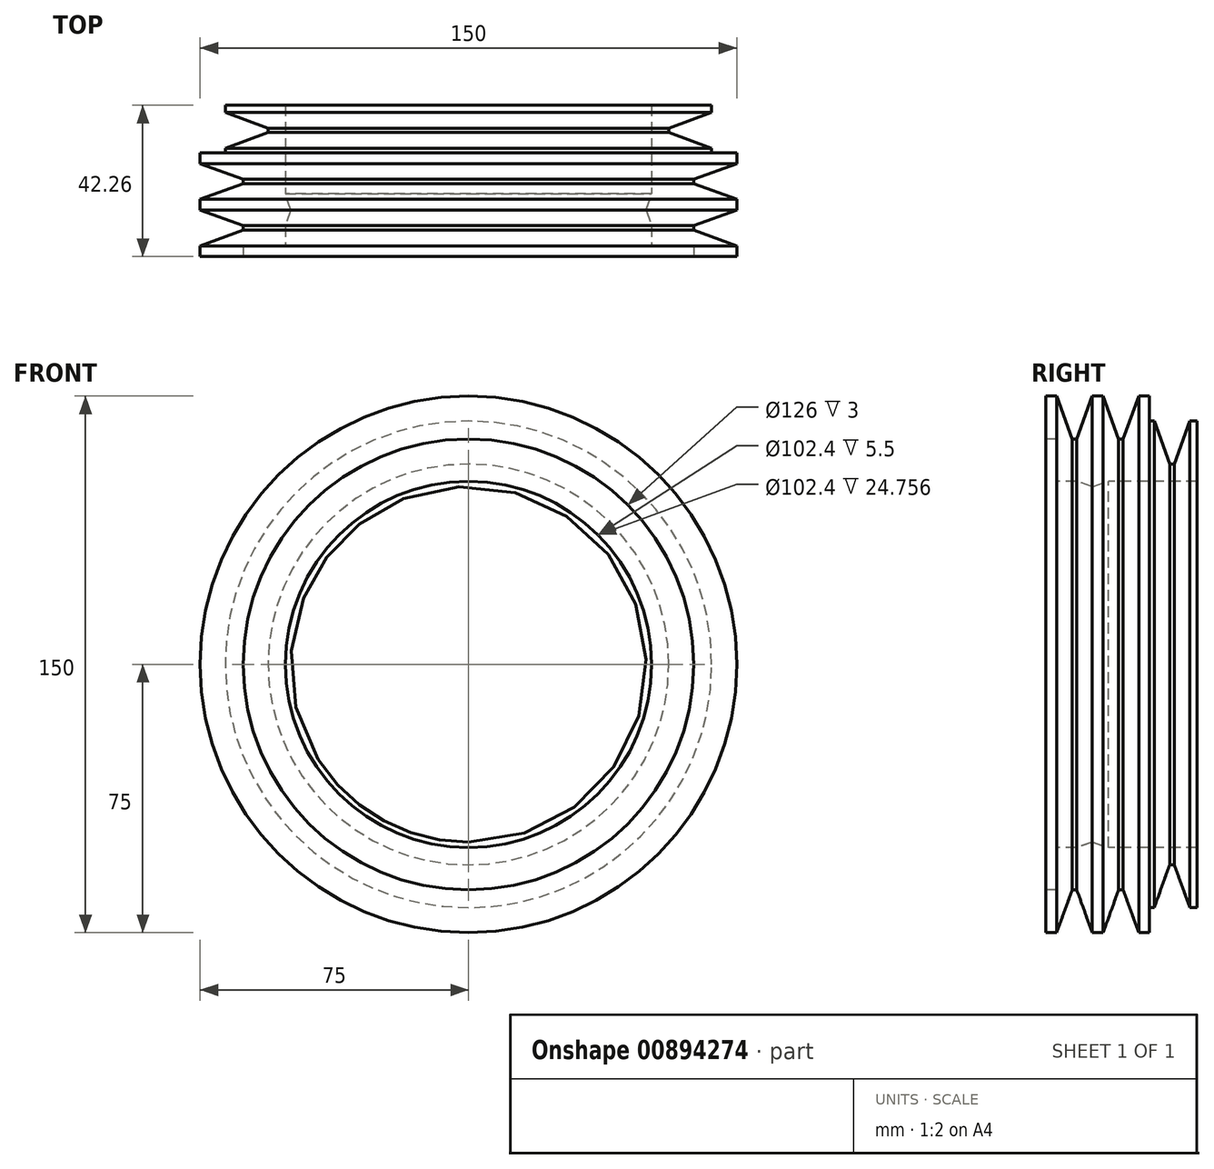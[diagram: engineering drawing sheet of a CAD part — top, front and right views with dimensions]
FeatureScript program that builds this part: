
annotation { "Feature Type Name" : "Feature", "Feature Type Description" : "" }
export const myFeature = defineFeature(function(context is Context, id is Id, definition is map)
    precondition{}
    {
        {
            var Q0;
            Q0=qCreatedBy(makeId("Right.planeOp"),FACE);
            var sketch = newSketch(context, id + "F0", { "sketchPlane" : qUnion([Q0])});
            skLineSegment(sketch, "E0", {"start": v(3, 51.2) * mm, "end": v(3, 63) * mm});
            skLineSegment(sketch, "E1", {"start": v(3, 63) * mm, "end": v(0, 63) * mm});
            skLineSegment(sketch, "E2", {"start": v(0, 63) * mm, "end": v(0, 75) * mm});
            skLineSegment(sketch, "E3", {"start": v(0, 75) * mm, "end": v(3, 75) * mm});
            skLineSegment(sketch, "E4", {"start": v(3, 75) * mm, "end": v(7.37, 63) * mm});
            skLineSegment(sketch, "E5", {"start": v(7.37, 63) * mm, "end": v(8.62, 63) * mm});
            skLineSegment(sketch, "E6", {"start": v(8.62, 63) * mm, "end": v(12.99, 75) * mm});
            skLineSegment(sketch, "E7", {"start": v(12.99, 75) * mm, "end": v(15.99, 75) * mm});
            skLineSegment(sketch, "E8", {"start": v(15.99, 75) * mm, "end": v(20.35, 63) * mm});
            skLineSegment(sketch, "E9", {"start": v(20.35, 63) * mm, "end": v(21.6, 63) * mm});
            skLineSegment(sketch, "E10", {"start": v(21.6, 63) * mm, "end": v(25.97, 75) * mm});
            skLineSegment(sketch, "E11", {"start": v(25.97, 75) * mm, "end": v(28.97, 75) * mm});
            skLineSegment(sketch, "E12", {"start": v(28.97, 75) * mm, "end": v(28.97, 68) * mm});
            skLineSegment(sketch, "E13", {"start": v(28.97, 68) * mm, "end": v(30.27, 68) * mm});
            skLineSegment(sketch, "E14", {"start": v(30.27, 68) * mm, "end": v(34.64, 56) * mm});
            skLineSegment(sketch, "E15", {"start": v(34.64, 56) * mm, "end": v(35.89, 56) * mm});
            skLineSegment(sketch, "E16", {"start": v(35.89, 56) * mm, "end": v(40.26, 68) * mm});
            skLineSegment(sketch, "E17", {"start": v(40.26, 68) * mm, "end": v(42.26, 68) * mm});
            skLineSegment(sketch, "E18", {"start": v(42.26, 68) * mm, "end": v(42.26, 51.2) * mm});
            skLineSegment(sketch, "E19", {"start": v(0, 0) * mm, "end": v(42.26, 0) * mm});
            skLineSegment(sketch, "E20", {"start": v(0, 63) * mm, "end": v(0, 0) * mm, "construction": true});
            skLineSegment(sketch, "E21", {"start": v(3, 75) * mm, "end": v(12.99, 75) * mm, "construction": true});
            skLineSegment(sketch, "E22", {"start": v(15.99, 75) * mm, "end": v(25.97, 75) * mm, "construction": true});
            skLineSegment(sketch, "E23", {"start": v(8, 75) * mm, "end": v(8, 63) * mm, "construction": true});
            skLineSegment(sketch, "E24", {"start": v(3, 51.2) * mm, "end": v(8.5, 51.2) * mm});
            skLineSegment(sketch, "E25", {"start": v(8.5, 51.2) * mm, "end": v(12.67, 49.76) * mm});
            skLineSegment(sketch, "E26", {"start": v(13.33, 49.76) * mm, "end": v(17.5, 51.2) * mm});
            skLineSegment(sketch, "E27", {"start": v(17.5, 51.2) * mm, "end": v(42.26, 51.2) * mm});
            skPoint(sketch, "E28.visualSharp", {"position": v(13, 49.64) * mm});
            skArc(sketch, "E28.filletArc", {"start": v(12.67, 49.76) * mm, "mid": v(13, 49.7) * mm, "end": v(13.33, 49.76) * mm});
            skSolve(sketch);
        }
        {
            var Q0;
            Q0=makeQuery(id+"F0.imprint","IMPRINT",FACE,{"disambiguationData":[TD([[makeQuery(id+"F0.imprint","IMPRINT",EDGE,{"derivedFrom":sQuery(id+"F0.wireOp",EDGE,"E0")}),-1.0]])]});
            var Q1;
            Q1=sQuery(id+"F0.wireOp",EDGE,"E19");
            revolve(context, id + "F1", {"surfaceOperationType" : NewSurfaceOperationType.NEW, "entities" : qUnion([Q0]), "axis" : qUnion([Q1]), "revolveType" : RevolveType.FULL});
        }
    });
